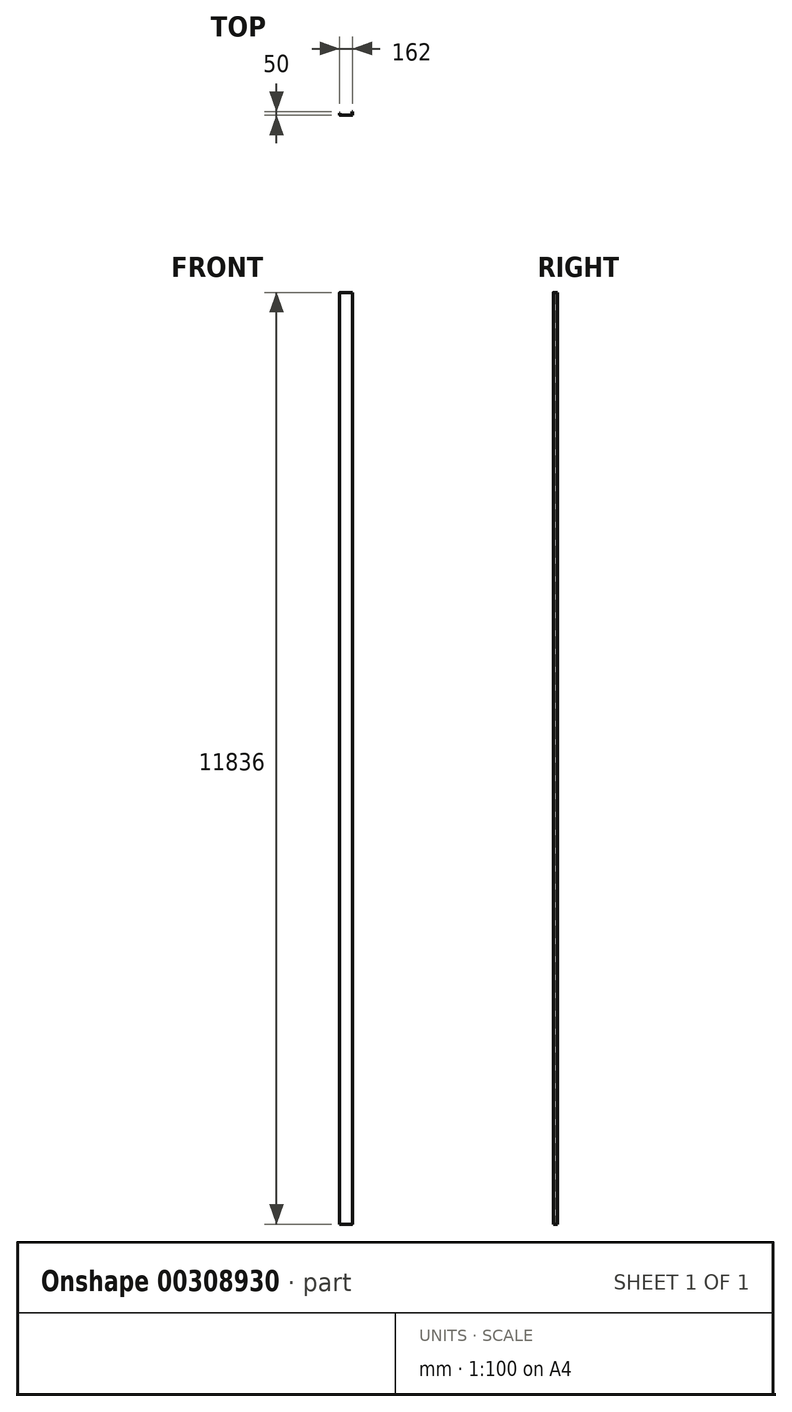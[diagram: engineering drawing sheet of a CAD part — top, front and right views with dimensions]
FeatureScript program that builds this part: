
annotation { "Feature Type Name" : "Feature", "Feature Type Description" : "" }
export const myFeature = defineFeature(function(context is Context, id is Id, definition is map)
    precondition{}
    {
        {
            var Q0;
            Q0=qCreatedBy(makeId("Top.planeOp"),FACE);
            var sketch = newSketch(context, id + "F0", { "sketchPlane" : qUnion([Q0])});
            skLineSegment(sketch, "E0", {"start": v(-29.3, 30) * mm, "end": v(-29.3, 6) * mm});
            skLineSegment(sketch, "E1", {"start": v(-23.3, 0) * mm, "end": v(126.7, 0) * mm});
            skLineSegment(sketch, "E2", {"start": v(132.7, 6) * mm, "end": v(132.7, 50) * mm});
            skLineSegment(sketch, "E3.0", {"start": v(128.7, 10) * mm, "end": v(128.7, 50) * mm});
            skLineSegment(sketch, "E3.1", {"start": v(-19.3, 4) * mm, "end": v(122.7, 4) * mm});
            skLineSegment(sketch, "E3.2", {"start": v(-25.3, 30) * mm, "end": v(-25.3, 10) * mm});
            skLineSegment(sketch, "E4", {"start": v(128.7, 50) * mm, "end": v(132.7, 50) * mm});
            skLineSegment(sketch, "E5", {"start": v(-29.3, 30) * mm, "end": v(-25.3, 30) * mm});
            skPoint(sketch, "E6.visualSharp", {"position": v(-25.3, 4) * mm});
            skArc(sketch, "E6.filletArc", {"start": v(-25.3, 10) * mm, "mid": v(-23.54, 5.76) * mm, "end": v(-19.3, 4) * mm});
            skPoint(sketch, "E7.visualSharp", {"position": v(128.7, 4) * mm});
            skArc(sketch, "E7.filletArc", {"start": v(122.7, 4) * mm, "mid": v(126.94, 5.76) * mm, "end": v(128.7, 10) * mm});
            skPoint(sketch, "E8.visualSharp", {"position": v(132.7, 0) * mm});
            skArc(sketch, "E8.filletArc", {"start": v(126.7, 0) * mm, "mid": v(130.94, 1.76) * mm, "end": v(132.7, 6) * mm});
            skPoint(sketch, "E9.visualSharp", {"position": v(-29.3, 0) * mm});
            skArc(sketch, "E9.filletArc", {"start": v(-29.3, 6) * mm, "mid": v(-27.54, 1.76) * mm, "end": v(-23.3, 0) * mm});
            skSolve(sketch);
        }
        {
            var Q0;
            Q0 = qSketchRegion(id + "F0", true);
            extrude(context, id + "F1", {"entities" : qUnion([Q0]), "depth" : 11836 * mm});
        }
    });
